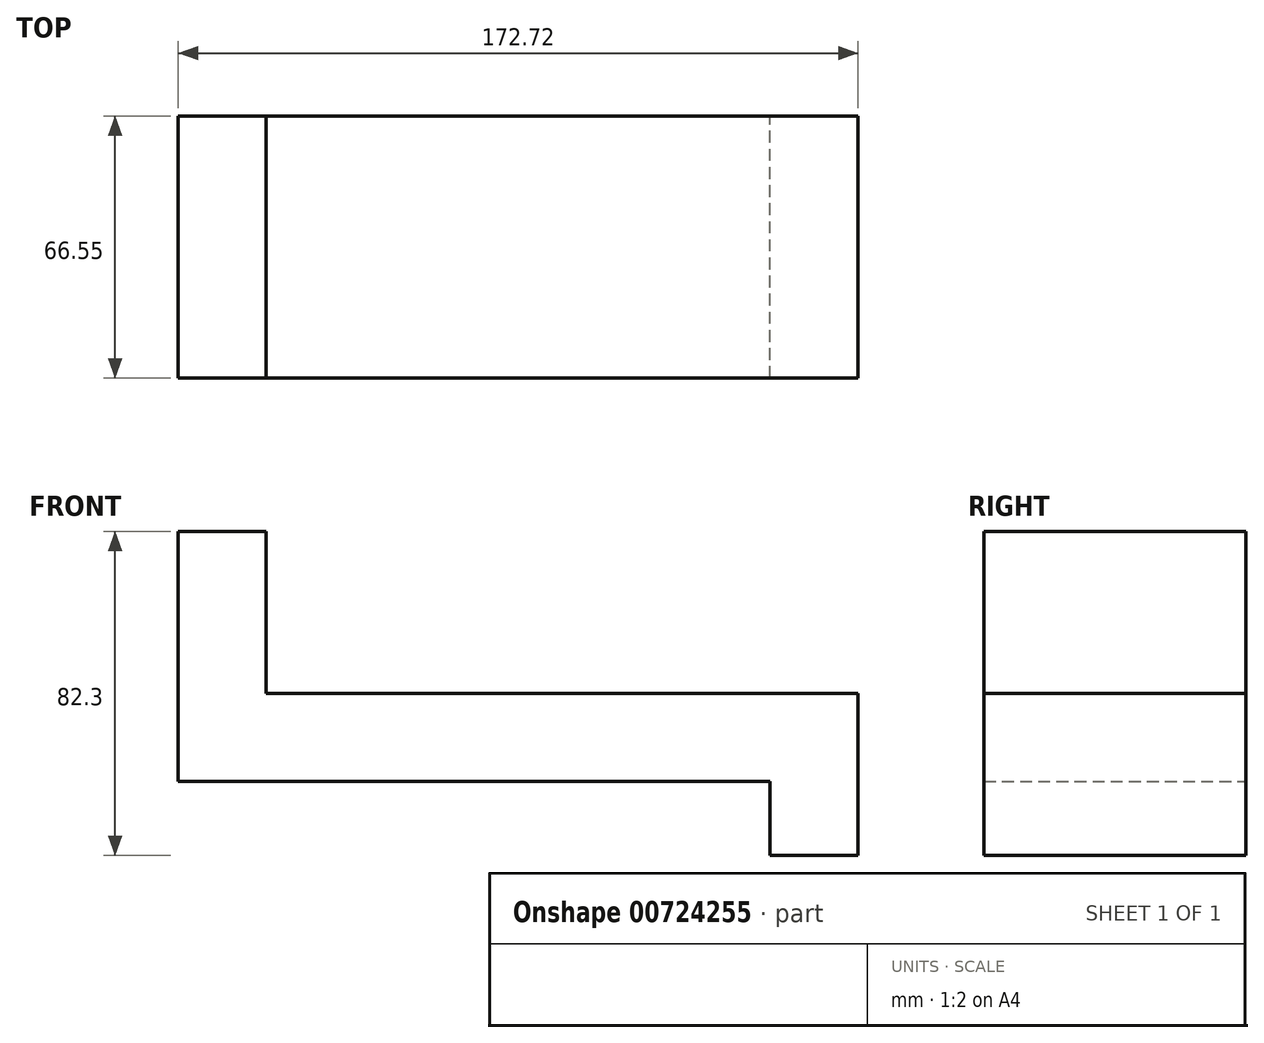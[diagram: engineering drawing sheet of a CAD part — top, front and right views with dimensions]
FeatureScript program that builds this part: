
annotation { "Feature Type Name" : "Feature", "Feature Type Description" : "" }
export const myFeature = defineFeature(function(context is Context, id is Id, definition is map)
    precondition{}
    {
        {
            var Q0;
            Q0=qCreatedBy(makeId("Front.planeOp"),FACE);
            var sketch = newSketch(context, id + "F0", { "sketchPlane" : qUnion([Q0])});
            skLineSegment(sketch, "E0", {"start": v(-118.6, 59) * mm, "end": v(-118.6, -4.5) * mm});
            skLineSegment(sketch, "E1", {"start": v(-118.6, -4.5) * mm, "end": v(31.77, -4.5) * mm});
            skLineSegment(sketch, "E2", {"start": v(31.77, -4.5) * mm, "end": v(31.77, -23.29) * mm});
            skLineSegment(sketch, "E3", {"start": v(31.77, -23.29) * mm, "end": v(54.12, -23.29) * mm});
            skLineSegment(sketch, "E4", {"start": v(54.12, -23.29) * mm, "end": v(54.12, 17.86) * mm});
            skLineSegment(sketch, "E5", {"start": v(54.12, 17.86) * mm, "end": v(-96.25, 17.86) * mm});
            skLineSegment(sketch, "E6", {"start": v(-96.25, 17.86) * mm, "end": v(-96.25, 59) * mm});
            skLineSegment(sketch, "E7", {"start": v(-96.25, 59) * mm, "end": v(-118.6, 59) * mm});
            skSolve(sketch);
        }
        {
            var Q0;
            Q0 = qSketchRegion(id + "F0", true);
            extrude(context, id + "F1", {"entities" : qUnion([Q0]), "depth" : 66.55 * mm, "offsetDistance" : 25.4 * mm});
        }
    });
